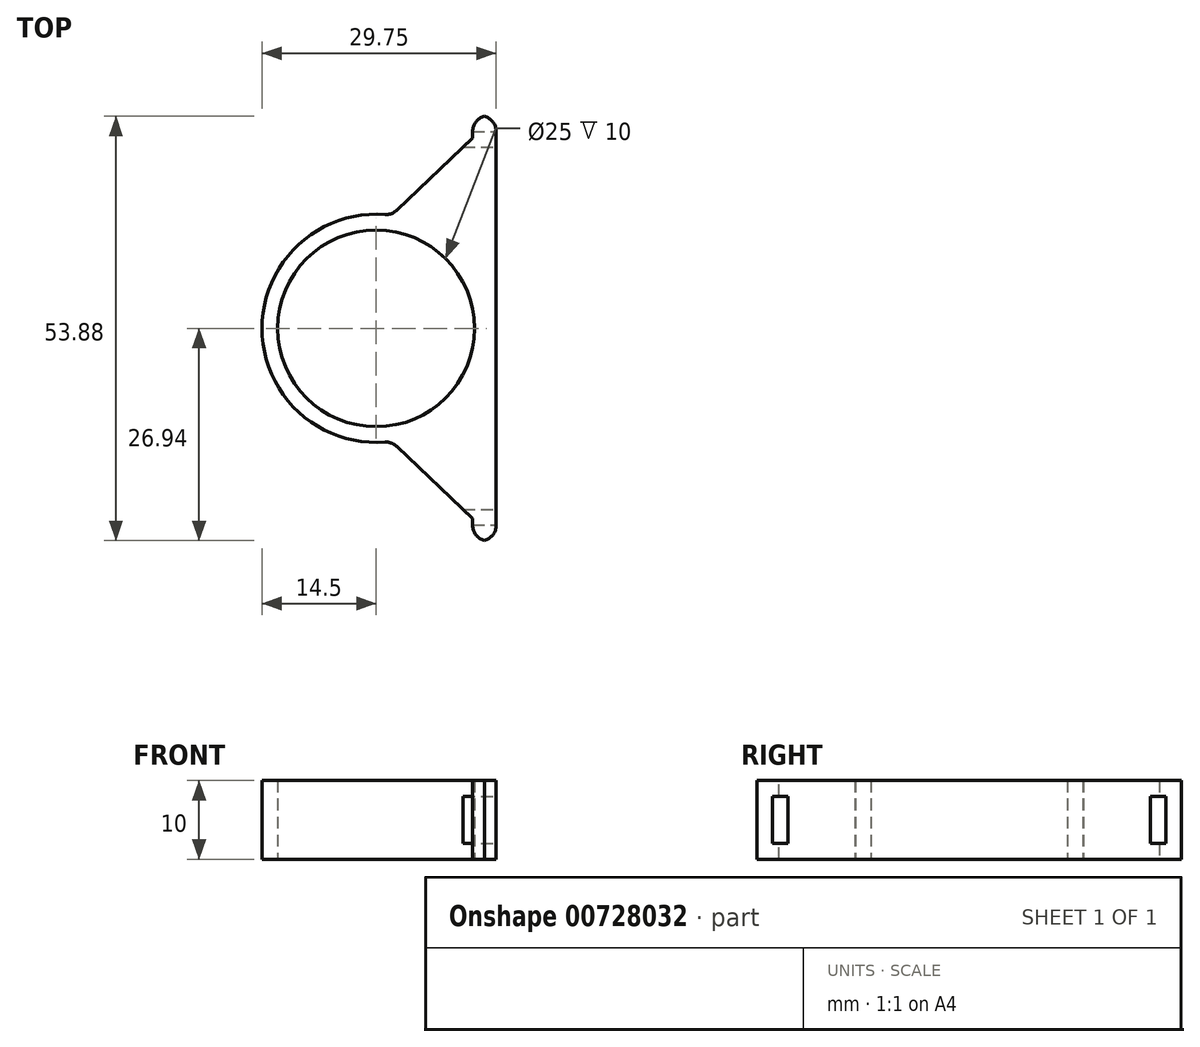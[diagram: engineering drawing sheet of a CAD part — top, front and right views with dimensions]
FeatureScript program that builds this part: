
annotation { "Feature Type Name" : "Feature", "Feature Type Description" : "" }
export const myFeature = defineFeature(function(context is Context, id is Id, definition is map)
    precondition{}
    {
        {
            var Q0;
            Q0=qCreatedBy(makeId("Top.planeOp"),FACE);
            var sketch = newSketch(context, id + "F0", { "sketchPlane" : qUnion([Q0])});
            skCircle(sketch, "E0", {"center": v(0, 0) * mm, "radius": 12.5 * mm});
            skCircle(sketch, "E1", {"center": v(0, 0) * mm, "radius": 14.5 * mm});
            skLineSegment(sketch, "E2", {"start": v(0, 12.5) * mm, "end": v(15.25, 27) * mm});
            skLineSegment(sketch, "E3", {"start": v(15.25, 27) * mm, "end": v(15.25, -27) * mm});
            skLineSegment(sketch, "E4", {"start": v(15.25, -27) * mm, "end": v(0, -12.5) * mm});
            skLineSegment(sketch, "E5", {"start": v(0, -12.5) * mm, "end": v(0, 12.5) * mm});
            skSolve(sketch);
        }
        {
            var Q0;
            Q0=makeQuery(id+"F0.imprint","IMPRINT",FACE,{"disambiguationData":[TD([[makeQuery(id+"F0.imprint","IMPRINT",EDGE,{"derivedFrom":sQuery(id+"F0.wireOp",EDGE,"E0")}),-1.0]])]});
            var Q1;
            {var subQ5=sQuery(id+"F0.wireOp",EDGE,"E3");Q1=makeQuery(id+"F0.imprint","IMPRINT",FACE,{"disambiguationData":[TD([[makeQuery(id+"F0.imprint","IMPRINT",EDGE,{"derivedFrom":subQ5}),-1.0]])]});}
            extrude(context, id + "F1", {"entities" : qUnion([Q0, Q1]), "endBound" : BoundingType.SYMMETRIC, "depth" : 10 * mm, "offsetDistance" : 25 * mm});
        }
        {
            var Q0;
            Q0=makeQuery(id+"F1.opExtrude","SWEPT_FACE",FACE,{"disambiguationData":[OSD([sQuery(id+"F0.wireOp",EDGE,"E3")])]});
            var sketch = newSketch(context, id + "F2", { "sketchPlane" : qUnion([Q0])});
            skLineSegment(sketch, "E6.bottom", {"start": v(23, 3) * mm, "end": v(25, 3) * mm});
            skLineSegment(sketch, "E6.top", {"start": v(23, -3) * mm, "end": v(25, -3) * mm});
            skLineSegment(sketch, "E6.left", {"start": v(23, 3) * mm, "end": v(23, -3) * mm});
            skLineSegment(sketch, "E6.right", {"start": v(25, 3) * mm, "end": v(25, -3) * mm});
            skLineSegment(sketch, "E7.MirrorCS", {"start": v(-23, 3) * mm, "end": v(-23, -3) * mm});
            skLineSegment(sketch, "E8.MirrorCS", {"start": v(-23, 3) * mm, "end": v(-25, 3) * mm});
            skLineSegment(sketch, "E9.MirrorCS", {"start": v(-25, 3) * mm, "end": v(-25, -3) * mm});
            skLineSegment(sketch, "E10.MirrorCS", {"start": v(-23, -3) * mm, "end": v(-25, -3) * mm});
            skSolve(sketch);
        }
        {
            var Q0;
            Q0=makeQuery(id+"F2.imprint","IMPRINT",FACE,{"disambiguationData":[TD([[makeQuery(id+"F2.imprint","IMPRINT",EDGE,{"derivedFrom":sQuery(id+"F2.wireOp",EDGE,"E7.MirrorCS")}),-1.0]])]});
            var Q1;
            Q1=makeQuery(id+"F2.imprint","IMPRINT",FACE,{"disambiguationData":[TD([[makeQuery(id+"F2.imprint","IMPRINT",EDGE,{"derivedFrom":sQuery(id+"F2.wireOp",EDGE,"E6.bottom")}),-1.0]])]});
            extrude(context, id + "F3", {"entities" : qUnion([Q0, Q1]), "operationType" : NewBodyOperationType.REMOVE, "oppositeDirection" : true, "depth" : 25 * mm, "offsetDistance" : 25 * mm});
        }
        {
            var Q0;
            Q0=makeQuery(id+"F1.opExtrude","SWEPT_FACE",FACE,{"disambiguationData":[OSD([sQuery(id+"F0.wireOp",EDGE,"E3")])]});
            extrude(context, id + "F4", {"entities" : qUnion([Q0]), "operationType" : NewBodyOperationType.ADD, "oppositeDirection" : true, "depth" : 3 * mm, "offsetDistance" : 25 * mm});
        }
        {
            var Q0;
            Q0=makeQuery(id+"F1.opExtrude","SWEPT_EDGE",EDGE,{"disambiguationData":[OSD([sQuery(id+"F0.wireOp",EDGE,"E1"),sQuery(id+"F0.wireOp",EDGE,"E4")])]});
            var Q1;
            Q1=makeQuery(id+"F1.opExtrude","SWEPT_EDGE",EDGE,{"disambiguationData":[OSD([sQuery(id+"F0.wireOp",EDGE,"E1"),sQuery(id+"F0.wireOp",EDGE,"E2")])]});
            var Q2;
            Q2=makeQuery(id+"F4.opExtrude","CAP_EDGE",EDGE,{"disambiguationData":[OSD([sQuery(id+"F0.wireOp",EDGE,"E3"),sQuery(id+"F0.wireOp",EDGE,"E4")])],"isStart":false});
            var Q3;
            Q3=makeQuery(id+"F4.opExtrude","CAP_EDGE",EDGE,{"disambiguationData":[OSD([sQuery(id+"F0.wireOp",EDGE,"E2"),sQuery(id+"F0.wireOp",EDGE,"E3")])],"isStart":false});
            var Q4;
            {var subQ0=sQuery(id+"F0.wireOp",EDGE,"E3");var subQ1=sQuery(id+"F0.wireOp",EDGE,"E2");Q4=makeQuery(id+"F4.boolean.opBoolean","MERGE",EDGE,{"derivedFrom":[makeQuery(id+"F1.opExtrude","SWEPT_EDGE",EDGE,{"disambiguationData":[OSD([subQ1,subQ0])]}),makeQuery(id+"F4.opExtrude","CAP_EDGE",EDGE,{"disambiguationData":[OSD([subQ1,subQ0])],"isStart":true})]});}
            var Q5;
            {var subQ0=sQuery(id+"F0.wireOp",EDGE,"E4");var subQ1=sQuery(id+"F0.wireOp",EDGE,"E3");Q5=makeQuery(id+"F4.boolean.opBoolean","MERGE",EDGE,{"derivedFrom":[makeQuery(id+"F1.opExtrude","SWEPT_EDGE",EDGE,{"disambiguationData":[OSD([subQ1,subQ0])]}),makeQuery(id+"F4.opExtrude","CAP_EDGE",EDGE,{"disambiguationData":[OSD([subQ1,subQ0])],"isStart":true})]});}
            fillet(context, id + "F5", {"entities" : qUnion([Q0, Q1, Q2, Q3, Q4, Q5]), "radius" : 2 * mm, "tangentPropagation" : true, "allowEdgeOverflow" : false});
        }
        {
            var Q0;
            {var subQ0=sQuery(id+"F0.wireOp",EDGE,"E5");Q0=makeQuery(id+"F0.imprint","IMPRINT",FACE,{"disambiguationData":[TD([[makeQuery(id+"F0.imprint","IMPRINT",EDGE,{"derivedFrom":subQ0}),-1.0]])]});}
            extrude(context, id + "F6", {"entities" : qUnion([Q0]), "operationType" : NewBodyOperationType.REMOVE, "endBound" : BoundingType.SYMMETRIC, "depth" : 25 * mm, "offsetDistance" : 25 * mm});
        }
    });
